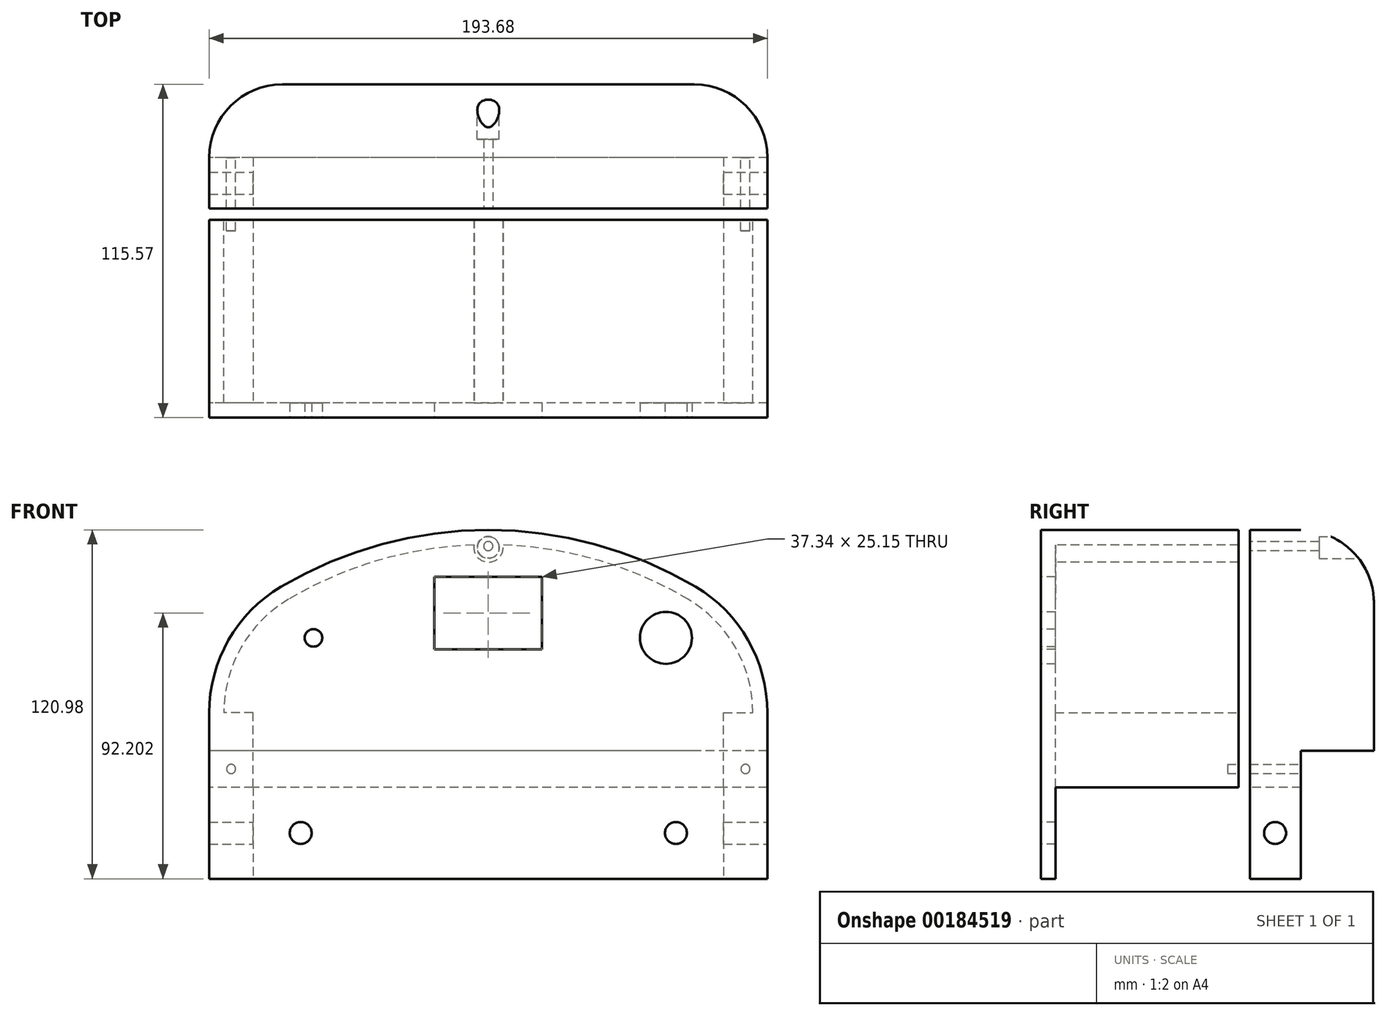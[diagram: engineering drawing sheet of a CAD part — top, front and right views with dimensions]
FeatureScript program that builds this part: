
annotation { "Feature Type Name" : "Feature", "Feature Type Description" : "" }
export const myFeature = defineFeature(function(context is Context, id is Id, definition is map)
    precondition{}
    {
        {
            var Q0;
            Q0=qCreatedBy(makeId("Front.planeOp"),FACE);
            var sketch = newSketch(context, id + "F0", { "sketchPlane" : qUnion([Q0])});
            skLineSegment(sketch, "E0.bottom", {"start": v(96.84, -25.4) * mm, "end": v(-96.84, -25.4) * mm});
            skLineSegment(sketch, "E0.top", {"start": v(96.84, 25.4) * mm, "end": v(-96.84, 25.4) * mm});
            skLineSegment(sketch, "E0.left", {"start": v(96.84, -25.4) * mm, "end": v(96.84, 25.4) * mm});
            skLineSegment(sketch, "E0.right", {"start": v(-96.84, -25.4) * mm, "end": v(-96.84, 25.4) * mm});
            skPoint(sketch, "E0.middle", {"position": v(0, 0) * mm});
            skCircle(sketch, "E1", {"center": v(0, -77.4) * mm, "radius": 141.24 * mm});
            skPoint(sketch, "E1.second.point", {"position": v(-3.23, 63.79) * mm});
            skSolve(sketch);
        }
        {
            var Q0;
            Q0=makeQuery(id+"F0.imprint","IMPRINT",FACE,{"disambiguationData":[TD([[makeQuery(id+"F0.imprint","IMPRINT",EDGE,{"derivedFrom":sQuery(id+"F0.wireOp",EDGE,"E0.bottom")}),-1.0]])]});
            var Q1;
            {var subQ0=sQuery(id+"F0.wireOp",EDGE,"E0.top");Q1=makeQuery(id+"F0.imprint","IMPRINT",FACE,{"disambiguationData":[TD([[makeQuery(id+"F0.imprint","IMPRINT",EDGE,{"derivedFrom":subQ0}),-1.0]])]});}
            extrude(context, id + "F1", {"entities" : qUnion([Q0, Q1]), "oppositeDirection" : true, "depth" : 114.3 * mm});
        }
        {
            var Q0;
            Q0=makeQuery(id+"F1.opExtrude","SWEPT_EDGE",EDGE,{"disambiguationData":[OSD([sQuery(id+"F0.wireOp",EDGE,"E0.top"),sQuery(id+"F0.wireOp",EDGE,"E0.left"),sQuery(id+"F0.wireOp",EDGE,"E1")])]});
            var Q1;
            Q1=makeQuery(id+"F1.opExtrude","SWEPT_EDGE",EDGE,{"disambiguationData":[OSD([sQuery(id+"F0.wireOp",EDGE,"E0.top"),sQuery(id+"F0.wireOp",EDGE,"E0.right"),sQuery(id+"F0.wireOp",EDGE,"E1")])]});
            fillet(context, id + "F2", {"entities" : qUnion([Q0, Q1]), "radius" : 50.8 * mm, "tangentPropagation" : true, "allowEdgeOverflow" : false});
        }
        {
            var Q0;
            {var subQ0=sQuery(id+"F0.wireOp",EDGE,"E0.top");Q0=makeQuery(id+"FWH5Dw56peIjbjm_0.boolean.opBoolean","MERGE",FACE,{"derivedFrom":[makeQuery(id+"F1.opExtrude","CAP_FACE",FACE,{"disambiguationData":[OSD([sQuery(id+"F0.wireOp",EDGE,"E0.bottom"),subQ0,sQuery(id+"F0.wireOp",EDGE,"E0.left"),sQuery(id+"F0.wireOp",EDGE,"E0.right")])],"isStart":true}),makeQuery(id+"FWH5Dw56peIjbjm_0.opExtrude","CAP_FACE",FACE,{"disambiguationData":[OSD([subQ0,sQuery(id+"F0.wireOp",EDGE,"E1")])],"isStart":true})]});}
            extrude(context, id + "F3", {"entities" : qUnion([Q0]), "operationType" : NewBodyOperationType.ADD, "depth" : 1.27 * mm});
        }
        {
            var Q0;
            Q0=makeQuery(id+"F3.opExtrude","CAP_FACE",FACE,{"disambiguationData":[OSD([sQuery(id+"F0.wireOp",EDGE,"E0.bottom"),sQuery(id+"F0.wireOp",EDGE,"E0.top"),sQuery(id+"F0.wireOp",EDGE,"E0.left"),sQuery(id+"F0.wireOp",EDGE,"E0.right"),sQuery(id+"F0.wireOp",EDGE,"E1")])],"isStart":false});
            var sketch = newSketch(context, id + "F4", { "sketchPlane" : qUnion([Q0])});
            skCircle(sketch, "E2", {"center": v(61.63, 26.42) * mm, "radius": 9.02 * mm});
            skSolve(sketch);
        }
        {
            var Q0;
            Q0=makeQuery(id+"F3.opExtrude","CAP_FACE",FACE,{"disambiguationData":[OSD([sQuery(id+"F0.wireOp",EDGE,"E0.bottom"),sQuery(id+"F0.wireOp",EDGE,"E0.top"),sQuery(id+"F0.wireOp",EDGE,"E0.left"),sQuery(id+"F0.wireOp",EDGE,"E0.right"),sQuery(id+"F0.wireOp",EDGE,"E1")])],"isStart":false});
            var sketch = newSketch(context, id + "F5", { "sketchPlane" : qUnion([Q0])});
            skLineSegment(sketch, "E3.bottom", {"start": v(18.67, 22.48) * mm, "end": v(-18.67, 22.48) * mm});
            skLineSegment(sketch, "E3.top", {"start": v(18.67, 47.63) * mm, "end": v(-18.67, 47.63) * mm});
            skLineSegment(sketch, "E3.left", {"start": v(18.67, 22.48) * mm, "end": v(18.67, 47.63) * mm});
            skLineSegment(sketch, "E3.right", {"start": v(-18.67, 22.48) * mm, "end": v(-18.67, 47.62) * mm});
            skPoint(sketch, "E3.middle", {"position": v(0, 0) * mm});
            skSolve(sketch);
        }
        {
            var Q0;
            Q0=makeQuery(id+"F3.opExtrude","CAP_FACE",FACE,{"disambiguationData":[OSD([sQuery(id+"F0.wireOp",EDGE,"E0.bottom"),sQuery(id+"F0.wireOp",EDGE,"E0.top"),sQuery(id+"F0.wireOp",EDGE,"E0.left"),sQuery(id+"F0.wireOp",EDGE,"E0.right"),sQuery(id+"F0.wireOp",EDGE,"E1")])],"isStart":false});
            var sketch = newSketch(context, id + "F6", { "sketchPlane" : qUnion([Q0])});
            skCircle(sketch, "E4", {"center": v(-66.36, -14.08) * mm, "radius": 3.81 * mm});
            skCircle(sketch, "E5.MirrorC", {"center": v(66.36, -14.08) * mm, "radius": 3.81 * mm});
            skSolve(sketch);
        }
        {
            var Q0;
            {var subQ0=sQuery(id+"F0.wireOp",EDGE,"E1");var subQ1=sQuery(id+"F0.wireOp",EDGE,"E0.left");Q0=makeQuery(id+"F2.opFillet","BLEND_EDGE",EDGE,{"blendedFrom":[makeQuery(id+"F1.opExtrude","SWEPT_EDGE",EDGE,{"disambiguationData":[OSD([sQuery(id+"F0.wireOp",EDGE,"E0.top"),subQ1,subQ0])]}),makeQuery(id+"F1.opExtrude","CAP_FACE",FACE,{"disambiguationData":[OSD([sQuery(id+"F0.wireOp",EDGE,"E0.bottom"),subQ1,sQuery(id+"F0.wireOp",EDGE,"E0.right"),subQ0])],"isStart":false})],"blendedInto":[makeQuery(id+"F1.opExtrude","CAP_FACE",FACE,{"disambiguationData":[OSD([sQuery(id+"F0.wireOp",EDGE,"E0.bottom"),subQ1,sQuery(id+"F0.wireOp",EDGE,"E0.right"),subQ0])],"isStart":false})]});}
            var Q1;
            Q1=makeQuery(id+"F1.opExtrude","CAP_EDGE",EDGE,{"disambiguationData":[OSD([sQuery(id+"F0.wireOp",EDGE,"E1")])],"isStart":false});
            var Q2;
            {var subQ0=sQuery(id+"F0.wireOp",EDGE,"E1");var subQ1=sQuery(id+"F0.wireOp",EDGE,"E0.right");Q2=makeQuery(id+"F2.opFillet","BLEND_EDGE",EDGE,{"blendedFrom":[makeQuery(id+"F1.opExtrude","SWEPT_EDGE",EDGE,{"disambiguationData":[OSD([sQuery(id+"F0.wireOp",EDGE,"E0.top"),subQ1,subQ0])]}),makeQuery(id+"F1.opExtrude","CAP_FACE",FACE,{"disambiguationData":[OSD([sQuery(id+"F0.wireOp",EDGE,"E0.bottom"),sQuery(id+"F0.wireOp",EDGE,"E0.left"),subQ1,subQ0])],"isStart":false})],"blendedInto":[makeQuery(id+"F1.opExtrude","CAP_FACE",FACE,{"disambiguationData":[OSD([sQuery(id+"F0.wireOp",EDGE,"E0.bottom"),sQuery(id+"F0.wireOp",EDGE,"E0.left"),subQ1,subQ0])],"isStart":false})]});}
            fillet(context, id + "F7", {"entities" : qUnion([Q0, Q1, Q2]), "radius" : 25.4 * mm, "tangentPropagation" : true, "allowEdgeOverflow" : false});
        }
        {
            var Q0;
            Q0=makeQuery(id+"F3.opExtrude","CAP_FACE",FACE,{"disambiguationData":[OSD([sQuery(id+"F0.wireOp",EDGE,"E0.bottom"),sQuery(id+"F0.wireOp",EDGE,"E0.left"),sQuery(id+"F0.wireOp",EDGE,"E0.right"),sQuery(id+"F0.wireOp",EDGE,"E1")])],"isStart":false});
            var sketch = newSketch(context, id + "F8", { "sketchPlane" : qUnion([Q0])});
            skCircle(sketch, "E6", {"center": v(-60.65, 26.42) * mm, "radius": 3.05 * mm});
            skSolve(sketch);
        }
        {
            var Q0;
            {var subQ0=sQuery(id+"F0.wireOp",EDGE,"E0.bottom");Q0=makeQuery(id+"F3.boolean.opBoolean","MERGE",FACE,{"derivedFrom":[makeQuery(id+"F1.opExtrude","SWEPT_FACE",FACE,{"disambiguationData":[OSD([subQ0])]}),makeQuery(id+"F3.opExtrude","SWEPT_FACE",FACE,{"disambiguationData":[OSD([subQ0])]})]});}
            var sketch = newSketch(context, id + "F9", { "sketchPlane" : qUnion([Q0])});
            skLineSegment(sketch, "E7", {"start": v(96.84, -67.31) * mm, "end": v(-96.84, -67.31) * mm});
            skLineSegment(sketch, "E8", {"start": v(96.84, -71.23) * mm, "end": v(-96.84, -71.23) * mm});
            skSolve(sketch);
        }
        {
            var Q0;
            {var subQ0=sQuery(id+"F9.wireOp",EDGE,"E7");Q0=makeQuery(id+"F9.imprint","IMPRINT",FACE,{"disambiguationData":[TD([[makeQuery(id+"F9.imprint","IMPRINT",EDGE,{"derivedFrom":subQ0}),1.0]])]});}
            extrude(context, id + "F10", {"entities" : qUnion([Q0]), "operationType" : NewBodyOperationType.REMOVE, "oppositeDirection" : true, "depth" : 127 * mm});
        }
        {
            var Q0;
            {var subQ0=sQuery(id+"F0.wireOp",EDGE,"E0.left");var subQ2=sQuery(id+"F0.wireOp",EDGE,"E0.bottom");Q0=makeQuery(id+"F10.boolean.opBoolean","SPLIT",FACE,{"disambiguationData":[TD([makeQuery(id+"F7.opFillet","BLEND_FACE",FACE,{"disambiguationData":[OSD([subQ0])]})])],"derivedFrom":makeQuery(id+"F3.boolean.opBoolean","MERGE",FACE,{"derivedFrom":[makeQuery(id+"F1.opExtrude","SWEPT_FACE",FACE,{"disambiguationData":[OSD([subQ2])]}),makeQuery(id+"F3.opExtrude","SWEPT_FACE",FACE,{"disambiguationData":[OSD([subQ2])]})]})});}
            var sketch = newSketch(context, id + "F11", { "sketchPlane" : qUnion([Q0])});
            skLineSegment(sketch, "E9", {"start": v(96.84, -88.9) * mm, "end": v(-96.84, -88.9) * mm});
            skSolve(sketch);
        }
        {
            var Q0;
            Q0=makeQuery(id+"F11.imprint","IMPRINT",FACE,{"disambiguationData":[TD([[makeQuery(id+"F11.imprint","IMPRINT",EDGE,{"derivedFrom":sQuery(id+"F11.wireOp",EDGE,"E9")}),-1.0]])]});
            extrude(context, id + "F12", {"entities" : qUnion([Q0]), "operationType" : NewBodyOperationType.ADD, "depth" : 31.75 * mm});
        }
        {
            var Q0;
            {var subQ2=sQuery(id+"F0.wireOp",EDGE,"E0.bottom");Q0=makeQuery(id+"F10.boolean.opBoolean","SPLIT",FACE,{"disambiguationData":[TD([makeQuery(id+"F10.opExtrude","SWEPT_FACE",FACE,{"disambiguationData":[OSD([sQuery(id+"F9.wireOp",EDGE,"E7")])]})])],"derivedFrom":makeQuery(id+"F3.boolean.opBoolean","MERGE",FACE,{"derivedFrom":[makeQuery(id+"F1.opExtrude","SWEPT_FACE",FACE,{"disambiguationData":[OSD([subQ2])]}),makeQuery(id+"F3.opExtrude","SWEPT_FACE",FACE,{"disambiguationData":[OSD([subQ2])]})]})});}
            var Q1;
            Q1=makeQuery(id+"F10.boolean.opBoolean","COPY",FACE,{"derivedFrom":makeQuery(id+"F10.opExtrude","SWEPT_FACE",FACE,{"disambiguationData":[OSD([sQuery(id+"F9.wireOp",EDGE,"E7")])]})});
            shell(context, id + "F13", {"entities" : qUnion([Q0, Q1]), "thickness" : 5.08 * mm});
        }
        {
            var Q0;
            {var subQ2=sQuery(id+"F0.wireOp",EDGE,"E0.bottom");Q0=makeQuery(id+"F10.boolean.opBoolean","SPLIT",FACE,{"disambiguationData":[TD([makeQuery(id+"F10.opExtrude","SWEPT_FACE",FACE,{"disambiguationData":[OSD([sQuery(id+"F9.wireOp",EDGE,"E7")])]})])],"derivedFrom":makeQuery(id+"F3.boolean.opBoolean","MERGE",FACE,{"derivedFrom":[makeQuery(id+"F1.opExtrude","SWEPT_FACE",FACE,{"disambiguationData":[OSD([subQ2])]}),makeQuery(id+"F3.opExtrude","SWEPT_FACE",FACE,{"disambiguationData":[OSD([subQ2])]})]})});}
            var sketch = newSketch(context, id + "F14", { "sketchPlane" : qUnion([Q0])});
            skLineSegment(sketch, "E10", {"start": v(-85.19, -3.81) * mm, "end": v(-96.84, -3.81) * mm});
            skLineSegment(sketch, "E11", {"start": v(-96.84, -3.81) * mm, "end": v(96.84, -3.81) * mm});
            skSolve(sketch);
        }
        {
            var Q0;
            {var subQ0=sQuery(id+"F0.wireOp",EDGE,"E0.bottom");var subQ1=makeQuery(id+"F3.opExtrude","CAP_EDGE",EDGE,{"disambiguationData":[OSD([subQ0])],"isStart":false});Q0=makeQuery(id+"F14.imprint","IMPRINT",FACE,{"disambiguationData":[TD([[makeQuery(id+"F14.imprint","IMPRINT",EDGE,{"derivedFrom":subQ1}),1.0]])]});}
            extrude(context, id + "F15", {"entities" : qUnion([Q0]), "operationType" : NewBodyOperationType.ADD, "depth" : 31.75 * mm});
        }
        {
            var Q0;
            Q0=makeQuery(id+"F13.opShell","OFFSET_FACE",FACE,{"disambiguationData":[OSD([sQuery(id+"F0.wireOp",EDGE,"E0.left")])]});
            extrude(context, id + "F16", {"entities" : qUnion([Q0]), "operationType" : NewBodyOperationType.ADD, "depth" : 10.16 * mm});
        }
        {
            var Q0;
            Q0=makeQuery(id+"F13.opShell","OFFSET_FACE",FACE,{"disambiguationData":[OSD([sQuery(id+"F0.wireOp",EDGE,"E0.right")])]});
            extrude(context, id + "F17", {"entities" : qUnion([Q0]), "operationType" : NewBodyOperationType.ADD, "depth" : 10.16 * mm});
        }
        {
            var Q0;
            {var subQ0=sQuery(id+"F0.wireOp",EDGE,"E0.bottom");Q0=makeQuery(id+"F15.boolean.opBoolean","MERGE",FACE,{"derivedFrom":[makeQuery(id+"F3.opExtrude","CAP_FACE",FACE,{"disambiguationData":[OSD([subQ0,sQuery(id+"F0.wireOp",EDGE,"E0.left"),sQuery(id+"F0.wireOp",EDGE,"E0.right"),sQuery(id+"F0.wireOp",EDGE,"E1")])],"isStart":false}),makeQuery(id+"F15.opExtrude","SWEPT_FACE",FACE,{"disambiguationData":[OSD([subQ0])]})]});}
            var sketch = newSketch(context, id + "F18", { "sketchPlane" : qUnion([Q0])});
            skCircle(sketch, "E12", {"center": v(-65.09, -41.27) * mm, "radius": 3.81 * mm});
            skCircle(sketch, "E13.MirrorC", {"center": v(65.09, -41.27) * mm, "radius": 3.81 * mm});
            skSolve(sketch);
        }
        {
            var Q0;
            Q0 = qSketchRegion(id + "F18", true);
            extrude(context, id + "F19", {"entities" : qUnion([Q0]), "operationType" : NewBodyOperationType.REMOVE, "oppositeDirection" : true, "depth" : 25.4 * mm});
        }
        {
            var Q0;
            Q0 = qSketchRegion(id + "F8", true);
            extrude(context, id + "F20", {"entities" : qUnion([Q0]), "operationType" : NewBodyOperationType.REMOVE, "oppositeDirection" : true, "depth" : 25.4 * mm});
        }
        {
            var Q0;
            Q0 = qSketchRegion(id + "F4", true);
            extrude(context, id + "F21", {"entities" : qUnion([Q0]), "operationType" : NewBodyOperationType.REMOVE, "oppositeDirection" : true, "depth" : 25.4 * mm});
        }
        {
            var Q0;
            Q0 = qSketchRegion(id + "F5", true);
            extrude(context, id + "F22", {"entities" : qUnion([Q0]), "operationType" : NewBodyOperationType.REMOVE, "oppositeDirection" : true, "depth" : 25.4 * mm});
        }
        {
            var Q0;
            Q0=makeQuery(id+"F6.imprint","IMPRINT",FACE,{"disambiguationData":[TD([[makeQuery(id+"F6.imprint","IMPRINT",EDGE,{"derivedFrom":sQuery(id+"F6.wireOp",EDGE,"E4")}),-1.0]])]});
            var sketch = newSketch(context, id + "F23", { "sketchPlane" : qUnion([Q0])});
            skCircle(sketch, "E14", {"center": v(0.06, 57.75) * mm, "radius": 5.08 * mm});
            skSolve(sketch);
        }
        {
            var Q0;
            Q0 = qSketchRegion(id + "F23", true);
            extrude(context, id + "F24", {"entities" : qUnion([Q0]), "operationType" : NewBodyOperationType.ADD, "oppositeDirection" : true, "depth" : 68.58 * mm});
        }
        {
            var Q0;
            {var subQ0=sQuery(id+"F9.wireOp",EDGE,"E8");Q0=makeQuery(id+"F12.boolean.opBoolean","MERGE",FACE,{"derivedFrom":[makeQuery(id+"F10.boolean.opBoolean","COPY",FACE,{"derivedFrom":makeQuery(id+"F10.opExtrude","SWEPT_FACE",FACE,{"disambiguationData":[OSD([subQ0])]})}),makeQuery(id+"F12.opExtrude","SWEPT_FACE",FACE,{"disambiguationData":[OSD([subQ0])]})]});}
            var sketch = newSketch(context, id + "F25", { "sketchPlane" : qUnion([Q0])});
            skCircle(sketch, "E15", {"center": v(0, 58.24) * mm, "radius": 1.59 * mm});
            skSolve(sketch);
        }
        {
            var Q0;
            Q0 = qSketchRegion(id + "F25", true);
            extrude(context, id + "F26", {"entities" : qUnion([Q0]), "operationType" : NewBodyOperationType.REMOVE, "oppositeDirection" : true, "depth" : 101.6 * mm});
        }
        {
            var Q0;
            Q0=makeQuery(id+"F1.opExtrude","CAP_FACE",FACE,{"disambiguationData":[OSD([sQuery(id+"F0.wireOp",EDGE,"E0.bottom"),sQuery(id+"F0.wireOp",EDGE,"E0.left"),sQuery(id+"F0.wireOp",EDGE,"E0.right"),sQuery(id+"F0.wireOp",EDGE,"E1")])],"isStart":false});
            var sketch = newSketch(context, id + "F27", { "sketchPlane" : qUnion([Q0])});
            skCircle(sketch, "E16", {"center": v(0, 57.75) * mm, "radius": 3.81 * mm});
            skSolve(sketch);
        }
        {
            var Q0;
            Q0 = qSketchRegion(id + "F27", true);
            extrude(context, id + "F28", {"entities" : qUnion([Q0]), "operationType" : NewBodyOperationType.REMOVE, "oppositeDirection" : true, "depth" : 19.05 * mm});
        }
        {
            var Q0;
            {var subQ0=sQuery(id+"F0.wireOp",EDGE,"E0.left");var subQ2=sQuery(id+"F0.wireOp",EDGE,"E0.bottom");Q0=makeQuery(id+"F10.boolean.opBoolean","SPLIT",FACE,{"disambiguationData":[TD([makeQuery(id+"F7.opFillet","BLEND_FACE",FACE,{"disambiguationData":[OSD([subQ0])]})])],"derivedFrom":makeQuery(id+"F3.boolean.opBoolean","MERGE",FACE,{"derivedFrom":[makeQuery(id+"F1.opExtrude","SWEPT_FACE",FACE,{"disambiguationData":[OSD([subQ2])]}),makeQuery(id+"F3.opExtrude","SWEPT_FACE",FACE,{"disambiguationData":[OSD([subQ2])]})]})});}
            extrude(context, id + "F29", {"entities" : qUnion([Q0]), "operationType" : NewBodyOperationType.REMOVE, "oppositeDirection" : true, "depth" : 12.7 * mm});
        }
        {
            var Q0;
            Q0=makeQuery(id+"F12.opExtrude","CAP_FACE",FACE,{"disambiguationData":[OSD([sQuery(id+"F0.wireOp",EDGE,"E0.bottom"),sQuery(id+"F0.wireOp",EDGE,"E0.left"),sQuery(id+"F0.wireOp",EDGE,"E0.right"),sQuery(id+"F9.wireOp",EDGE,"E8"),sQuery(id+"F11.wireOp",EDGE,"E9")])],"isStart":false});
            var sketch = newSketch(context, id + "F30", { "sketchPlane" : qUnion([Q0])});
            skLineSegment(sketch, "E17", {"start": v(81.6, -88.9) * mm, "end": v(81.6, -71.23) * mm});
            skSolve(sketch);
        }
        {
            var Q0;
            {var subQ0=sQuery(id+"F30.wireOp",EDGE,"E17");Q0=makeQuery(id+"F30.imprint","IMPRINT",FACE,{"disambiguationData":[TD([[makeQuery(id+"F30.imprint","IMPRINT",EDGE,{"derivedFrom":subQ0}),1.0]])]});}
            var sketch = newSketch(context, id + "F31", { "sketchPlane" : qUnion([Q0])});
            skLineSegment(sketch, "E18", {"start": v(-81.6, -88.99) * mm, "end": v(-81.6, -70.88) * mm});
            skSolve(sketch);
        }
        {
            var Q0;
            {var subQ3=sQuery(id+"F30.wireOp",EDGE,"E17");var subQ9=makeQuery(id+"F30.imprint","IMPRINT",EDGE,{"derivedFrom":subQ3});Q0=makeQuery(id+"F31.imprint","IMPRINT",FACE,{"disambiguationData":[TD([[makeQuery(id+"F31.imprint","IMPRINT",EDGE,{"derivedFrom":subQ9}),1.0]])]});}
            extrude(context, id + "F32", {"entities" : qUnion([Q0]), "operationType" : NewBodyOperationType.REMOVE, "oppositeDirection" : true, "depth" : 31.75 * mm});
        }
        {
            var Q0;
            {var subQ0=sQuery(id+"F11.wireOp",EDGE,"E9");Q0=makeQuery(id+"F29.boolean.opBoolean","MERGE",FACE,{"derivedFrom":[makeQuery(id+"F12.opExtrude","SWEPT_FACE",FACE,{"disambiguationData":[OSD([subQ0])]}),makeQuery(id+"F29.opExtrude","SWEPT_FACE",FACE,{"disambiguationData":[OSD([subQ0])]})]});}
            var sketch = newSketch(context, id + "F33", { "sketchPlane" : qUnion([Q0])});
            skCircle(sketch, "E19", {"center": v(-89.22, -19.05) * mm, "radius": 1.59 * mm});
            skSolve(sketch);
        }
        {
            var Q0;
            Q0=makeQuery(id+"F33.imprint","IMPRINT",FACE,{"disambiguationData":[TD([[makeQuery(id+"F33.imprint","IMPRINT",EDGE,{"derivedFrom":sQuery(id+"F33.wireOp",EDGE,"E19")}),-1.0]])]});
            var sketch = newSketch(context, id + "F34", { "sketchPlane" : qUnion([Q0])});
            skCircle(sketch, "E20", {"center": v(89.22, -19.05) * mm, "radius": 1.59 * mm});
            skSolve(sketch);
        }
        {
            var Q0;
            Q0 = qSketchRegion(id + "F34", true);
            extrude(context, id + "F35", {"entities" : qUnion([Q0]), "operationType" : NewBodyOperationType.REMOVE, "oppositeDirection" : true, "depth" : 25.4 * mm});
        }
        {
            var Q0;
            Q0 = qSketchRegion(id + "F33", true);
            extrude(context, id + "F36", {"entities" : qUnion([Q0]), "operationType" : NewBodyOperationType.REMOVE, "oppositeDirection" : true, "depth" : 25.4 * mm});
        }
        {
            var Q0;
            {var subQ0=sQuery(id+"F0.wireOp",EDGE,"E0.left");var subQ1=sQuery(id+"F0.wireOp",EDGE,"E0.bottom");Q0=makeQuery(id+"F12.boolean.opBoolean","MERGE",FACE,{"derivedFrom":[makeQuery(id+"F10.boolean.opBoolean","SPLIT",FACE,{"disambiguationData":[TD([makeQuery(id+"F7.opFillet","BLEND_FACE",FACE,{"disambiguationData":[OSD([subQ0])]})])],"derivedFrom":makeQuery(id+"F3.boolean.opBoolean","MERGE",FACE,{"derivedFrom":[makeQuery(id+"F1.opExtrude","SWEPT_FACE",FACE,{"disambiguationData":[OSD([subQ0])]}),makeQuery(id+"F3.opExtrude","SWEPT_FACE",FACE,{"disambiguationData":[OSD([subQ0])]})]})}),makeQuery(id+"F12.opExtrude","SWEPT_FACE",FACE,{"disambiguationData":[OSD([subQ1,subQ0])]})]});}
            var sketch = newSketch(context, id + "F37", { "sketchPlane" : qUnion([Q0])});
            skCircle(sketch, "E21", {"center": v(80.01, -41.27) * mm, "radius": 3.81 * mm});
            skSolve(sketch);
        }
        {
            var Q0;
            Q0 = qSketchRegion(id + "F37", true);
            extrude(context, id + "F38", {"entities" : qUnion([Q0]), "operationType" : NewBodyOperationType.REMOVE, "oppositeDirection" : true, "depth" : 254 * mm});
        }
    });
